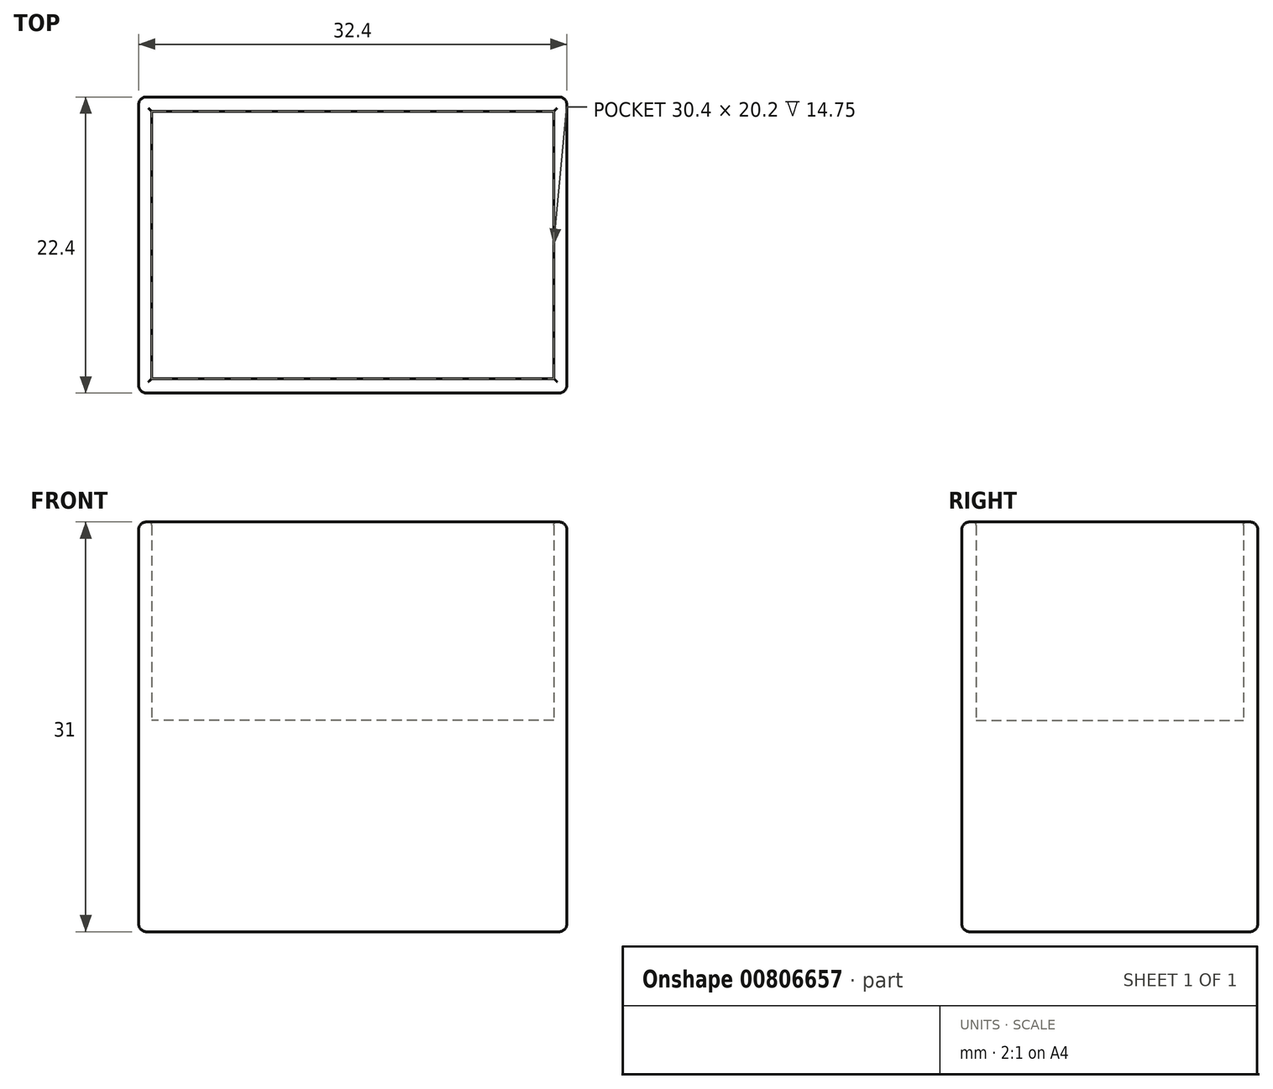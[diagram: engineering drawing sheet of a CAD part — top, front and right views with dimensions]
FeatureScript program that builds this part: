
annotation { "Feature Type Name" : "Feature", "Feature Type Description" : "" }
export const myFeature = defineFeature(function(context is Context, id is Id, definition is map)
    precondition{}
    {
        {
            var Q0;
            Q0=qCreatedBy(makeId("Top.planeOp"),FACE);
            var sketch = newSketch(context, id + "F0", { "sketchPlane" : qUnion([Q0])});
            skLineSegment(sketch, "E0.bottom", {"start": v(15.2, -10.1) * mm, "end": v(-15.2, -10.1) * mm});
            skLineSegment(sketch, "E0.top", {"start": v(15.2, 10.1) * mm, "end": v(-15.2, 10.1) * mm});
            skLineSegment(sketch, "E0.left", {"start": v(15.2, -10.1) * mm, "end": v(15.2, 10.1) * mm});
            skLineSegment(sketch, "E0.right", {"start": v(-15.2, -10.1) * mm, "end": v(-15.2, 10.1) * mm});
            skPoint(sketch, "E0.middle", {"position": v(0, 0) * mm});
            skLineSegment(sketch, "E1.bottom", {"start": v(16.2, -11.2) * mm, "end": v(-16.2, -11.2) * mm});
            skLineSegment(sketch, "E1.top", {"start": v(16.2, 11.2) * mm, "end": v(-16.2, 11.2) * mm});
            skLineSegment(sketch, "E1.left", {"start": v(16.2, -11.2) * mm, "end": v(16.2, 11.2) * mm});
            skLineSegment(sketch, "E1.right", {"start": v(-16.2, -11.2) * mm, "end": v(-16.2, 11.2) * mm});
            skSolve(sketch);
        }
        {
            var Q0;
            Q0=makeQuery(id+"F0.imprint","IMPRINT",FACE,{"disambiguationData":[TD([[makeQuery(id+"F0.imprint","IMPRINT",EDGE,{"derivedFrom":sQuery(id+"F0.wireOp",EDGE,"E0.bottom")}),-1.0]])]});
            extrude(context, id + "F1", {"entities" : qUnion([Q0]), "oppositeDirection" : true, "depth" : 16 * mm, "offsetDistance" : 25 * mm});
        }
        {
            var Q0;
            Q0=makeQuery(id+"F0.imprint","IMPRINT",FACE,{"disambiguationData":[TD([[makeQuery(id+"F0.imprint","IMPRINT",EDGE,{"derivedFrom":sQuery(id+"F0.wireOp",EDGE,"E0.bottom")}),1.0]])]});
            extrude(context, id + "F2", {"entities" : qUnion([Q0]), "operationType" : NewBodyOperationType.ADD, "oppositeDirection" : true, "depth" : 16 * mm, "offsetDistance" : 25 * mm});
        }
        {
            var Q0;
            Q0=makeQuery(id+"F0.imprint","IMPRINT",FACE,{"disambiguationData":[TD([[makeQuery(id+"F0.imprint","IMPRINT",EDGE,{"derivedFrom":sQuery(id+"F0.wireOp",EDGE,"E0.bottom")}),1.0]])]});
            extrude(context, id + "F3", {"entities" : qUnion([Q0]), "operationType" : NewBodyOperationType.ADD, "depth" : 15 * mm, "offsetDistance" : 25 * mm});
        }
        {
            var Q0;
            Q0=makeQuery(id+"F3.opExtrude","CAP_EDGE",EDGE,{"disambiguationData":[OSD([sQuery(id+"F0.wireOp",EDGE,"E0.right")])],"isStart":false});
            fillet(context, id + "F4", {"entities" : qUnion([Q0]), "radius" : 0.25 * mm, "tangentPropagation" : true, "allowEdgeOverflow" : false});
        }
        {
            var Q0;
            Q0=makeQuery(id+"F3.opExtrude","CAP_EDGE",EDGE,{"disambiguationData":[OSD([sQuery(id+"F0.wireOp",EDGE,"E0.top")])],"isStart":false});
            var Q1;
            Q1=makeQuery(id+"F3.opExtrude","CAP_EDGE",EDGE,{"disambiguationData":[OSD([sQuery(id+"F0.wireOp",EDGE,"E0.left")])],"isStart":false});
            var Q2;
            Q2=makeQuery(id+"F3.opExtrude","CAP_EDGE",EDGE,{"disambiguationData":[OSD([sQuery(id+"F0.wireOp",EDGE,"E0.bottom")])],"isStart":false});
            fillet(context, id + "F5", {"entities" : qUnion([Q0, Q1, Q2]), "radius" : 0.25 * mm, "tangentPropagation" : true, "allowEdgeOverflow" : false});
        }
        {
            var Q0;
            Q0=makeQuery(id+"F3.opExtrude","CAP_EDGE",EDGE,{"disambiguationData":[OSD([sQuery(id+"F0.wireOp",EDGE,"E1.bottom")])],"isStart":false});
            var Q1;
            Q1=makeQuery(id+"F3.opExtrude","CAP_EDGE",EDGE,{"disambiguationData":[OSD([sQuery(id+"F0.wireOp",EDGE,"E1.right")])],"isStart":false});
            var Q2;
            Q2=makeQuery(id+"F3.opExtrude","CAP_EDGE",EDGE,{"disambiguationData":[OSD([sQuery(id+"F0.wireOp",EDGE,"E1.top")])],"isStart":false});
            var Q3;
            Q3=makeQuery(id+"F3.opExtrude","CAP_EDGE",EDGE,{"disambiguationData":[OSD([sQuery(id+"F0.wireOp",EDGE,"E1.left")])],"isStart":false});
            var Q4;
            {var subQ0=sQuery(id+"F0.wireOp",EDGE,"E1.right");var subQ1=sQuery(id+"F0.wireOp",EDGE,"E1.bottom");Q4=makeQuery(id+"F3.boolean.opBoolean","MERGE",EDGE,{"derivedFrom":[makeQuery(id+"F2.opExtrude","SWEPT_EDGE",EDGE,{"disambiguationData":[OSD([subQ1,subQ0])]}),makeQuery(id+"F3.opExtrude","SWEPT_EDGE",EDGE,{"disambiguationData":[OSD([subQ1,subQ0])]})]});}
            var Q5;
            {var subQ0=sQuery(id+"F0.wireOp",EDGE,"E1.left");var subQ1=sQuery(id+"F0.wireOp",EDGE,"E1.bottom");Q5=makeQuery(id+"F3.boolean.opBoolean","MERGE",EDGE,{"derivedFrom":[makeQuery(id+"F2.opExtrude","SWEPT_EDGE",EDGE,{"disambiguationData":[OSD([subQ1,subQ0])]}),makeQuery(id+"F3.opExtrude","SWEPT_EDGE",EDGE,{"disambiguationData":[OSD([subQ1,subQ0])]})]});}
            var Q6;
            {var subQ0=sQuery(id+"F0.wireOp",EDGE,"E1.left");var subQ1=sQuery(id+"F0.wireOp",EDGE,"E1.top");Q6=makeQuery(id+"F3.boolean.opBoolean","MERGE",EDGE,{"derivedFrom":[makeQuery(id+"F2.opExtrude","SWEPT_EDGE",EDGE,{"disambiguationData":[OSD([subQ1,subQ0])]}),makeQuery(id+"F3.opExtrude","SWEPT_EDGE",EDGE,{"disambiguationData":[OSD([subQ1,subQ0])]})]});}
            var Q7;
            {var subQ0=sQuery(id+"F0.wireOp",EDGE,"E1.right");var subQ1=sQuery(id+"F0.wireOp",EDGE,"E1.top");Q7=makeQuery(id+"F3.boolean.opBoolean","MERGE",EDGE,{"derivedFrom":[makeQuery(id+"F2.opExtrude","SWEPT_EDGE",EDGE,{"disambiguationData":[OSD([subQ1,subQ0])]}),makeQuery(id+"F3.opExtrude","SWEPT_EDGE",EDGE,{"disambiguationData":[OSD([subQ1,subQ0])]})]});}
            var Q8;
            Q8=makeQuery(id+"F2.opExtrude","CAP_EDGE",EDGE,{"disambiguationData":[OSD([sQuery(id+"F0.wireOp",EDGE,"E1.bottom")])],"isStart":false});
            var Q9;
            Q9=makeQuery(id+"F2.opExtrude","CAP_EDGE",EDGE,{"disambiguationData":[OSD([sQuery(id+"F0.wireOp",EDGE,"E1.left")])],"isStart":false});
            var Q10;
            Q10=makeQuery(id+"F2.opExtrude","CAP_EDGE",EDGE,{"disambiguationData":[OSD([sQuery(id+"F0.wireOp",EDGE,"E1.top")])],"isStart":false});
            var Q11;
            Q11=makeQuery(id+"F2.opExtrude","CAP_EDGE",EDGE,{"disambiguationData":[OSD([sQuery(id+"F0.wireOp",EDGE,"E1.right")])],"isStart":false});
            fillet(context, id + "F6", {"entities" : qUnion([Q0, Q1, Q2, Q3, Q4, Q5, Q6, Q7, Q8, Q9, Q10, Q11]), "radius" : 0.6 * mm, "tangentPropagation" : true, "allowEdgeOverflow" : false});
        }
    });
